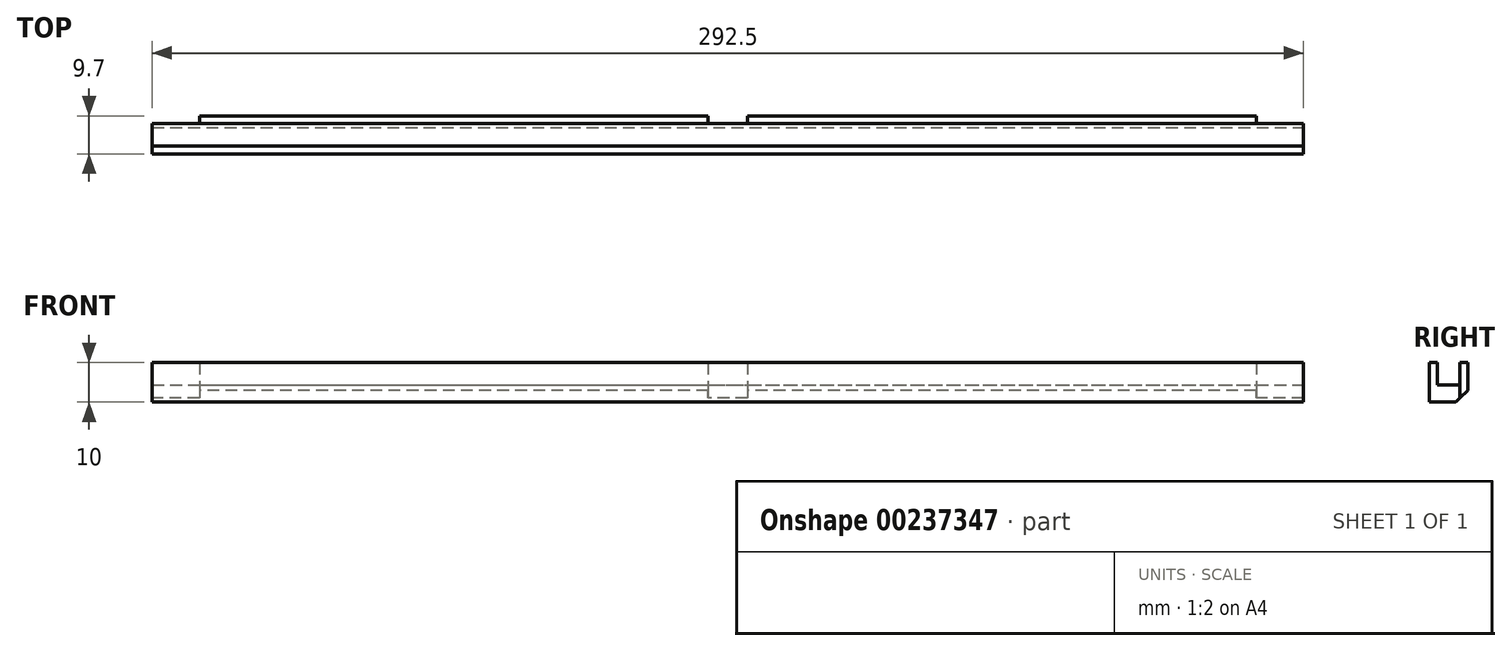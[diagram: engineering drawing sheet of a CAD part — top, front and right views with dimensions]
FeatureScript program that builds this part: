
annotation { "Feature Type Name" : "Feature", "Feature Type Description" : "" }
export const myFeature = defineFeature(function(context is Context, id is Id, definition is map)
    precondition{}
    {
        {
            var Q0;
            Q0=qCreatedBy(makeId("Top.planeOp"),FACE);
            var sketch = newSketch(context, id + "F0", { "sketchPlane" : qUnion([Q0])});
            skLineSegment(sketch, "E0.bottom", {"start": v(-146.25, 2.85) * mm, "end": v(146.25, 2.85) * mm});
            skLineSegment(sketch, "E0.top", {"start": v(-146.25, -2.85) * mm, "end": v(146.25, -2.85) * mm});
            skLineSegment(sketch, "E0.left", {"start": v(-146.25, 2.85) * mm, "end": v(-146.25, -2.85) * mm});
            skLineSegment(sketch, "E0.right", {"start": v(146.25, 2.85) * mm, "end": v(146.25, -2.85) * mm});
            skPoint(sketch, "E0.middle", {"position": v(0, 0) * mm});
            skLineSegment(sketch, "E1", {"start": v(-146.25, 2.85) * mm, "end": v(-146.25, 4.85) * mm});
            skLineSegment(sketch, "E2", {"start": v(-146.25, 4.85) * mm, "end": v(146.25, 4.85) * mm});
            skLineSegment(sketch, "E3", {"start": v(146.25, 4.85) * mm, "end": v(146.25, 2.85) * mm});
            skLineSegment(sketch, "E4", {"start": v(-146.25, -2.85) * mm, "end": v(-146.25, -4.85) * mm});
            skLineSegment(sketch, "E5", {"start": v(-146.25, -4.85) * mm, "end": v(146.25, -4.85) * mm});
            skLineSegment(sketch, "E6", {"start": v(146.25, -4.85) * mm, "end": v(146.25, -2.85) * mm});
            skLineSegment(sketch, "E7", {"start": v(0, 4.85) * mm, "end": v(0, -4.85) * mm});
            skLineSegment(sketch, "E8.bottom", {"start": v(-139.25, 2.85) * mm, "end": v(-134.25, 2.85) * mm});
            skLineSegment(sketch, "E8.top", {"start": v(-139.25, 4.85) * mm, "end": v(-134.25, 4.85) * mm});
            skLineSegment(sketch, "E8.left", {"start": v(-139.25, 2.85) * mm, "end": v(-139.25, 4.85) * mm});
            skLineSegment(sketch, "E8.right", {"start": v(-134.25, 2.85) * mm, "end": v(-134.25, 4.85) * mm});
            skLineSegment(sketch, "E9.MirrorCS", {"start": v(139.25, 2.85) * mm, "end": v(134.25, 2.85) * mm});
            skLineSegment(sketch, "E10.MirrorCS", {"start": v(139.25, 4.85) * mm, "end": v(134.25, 4.85) * mm});
            skLineSegment(sketch, "E11.MirrorCS", {"start": v(139.25, 2.85) * mm, "end": v(139.25, 4.85) * mm});
            skLineSegment(sketch, "E12.MirrorCS", {"start": v(134.25, 2.85) * mm, "end": v(134.25, 4.85) * mm});
            skLineSegment(sketch, "E13.bottom", {"start": v(5, 2.85) * mm, "end": v(-5, 2.85) * mm});
            skLineSegment(sketch, "E13.left", {"start": v(5, 2.85) * mm, "end": v(5, 4.85) * mm});
            skLineSegment(sketch, "E13.right", {"start": v(-5, 2.85) * mm, "end": v(-5, 4.85) * mm});
            skPoint(sketch, "E13.middle", {"position": v(0, 4.85) * mm});
            skLineSegment(sketch, "E14", {"start": v(-139.25, 4.85) * mm, "end": v(-139.25, 2.85) * mm});
            skLineSegment(sketch, "E15.MirrorCS", {"start": v(139.25, 4.85) * mm, "end": v(139.25, 2.85) * mm});
            skSolve(sketch);
        }
        {
            var Q0;
            {var subQ0=sQuery(id+"F0.wireOp",EDGE,"E0.right");Q0=makeQuery(id+"F0.imprint","IMPRINT",FACE,{"disambiguationData":[TD([[makeQuery(id+"F0.imprint","IMPRINT",EDGE,{"derivedFrom":subQ0}),-1.0]])]});}
            var Q1;
            {var subQ0=sQuery(id+"F0.wireOp",EDGE,"1EJgJWwb-nkAs-t9n1-ytm8-ceu9wyUzjA9J.bottom");Q1=makeQuery(id+"F0.imprint","IMPRINT",FACE,{"disambiguationData":[TD([[makeQuery(id+"F0.imprint","IMPRINT",EDGE,{"derivedFrom":subQ0}),-1.0]])]});}
            var Q2;
            {var subQ6=sQuery(id+"F0.wireOp",EDGE,"E0.left");Q2=makeQuery(id+"F0.imprint","IMPRINT",FACE,{"disambiguationData":[TD([[makeQuery(id+"F0.imprint","IMPRINT",EDGE,{"derivedFrom":subQ6}),1.0]])]});}
            extrude(context, id + "F1", {"entities" : qUnion([Q0, Q1, Q2]), "depth" : 4.3 * mm});
        }
        {
            var Q0;
            {var subQ0=sQuery(id+"F0.wireOp",EDGE,"E12.MirrorCS");Q0=makeQuery(id+"F0.imprint","IMPRINT",FACE,{"disambiguationData":[TD([[makeQuery(id+"F0.imprint","IMPRINT",EDGE,{"derivedFrom":subQ0}),1.0]])]});}
            var Q1;
            {var subQ0=sQuery(id+"F0.wireOp",EDGE,"E6");Q1=makeQuery(id+"F0.imprint","IMPRINT",FACE,{"disambiguationData":[TD([[makeQuery(id+"F0.imprint","IMPRINT",EDGE,{"derivedFrom":subQ0}),1.0]])]});}
            var Q2;
            {var subQ0=sQuery(id+"F0.wireOp",EDGE,"E4");Q2=makeQuery(id+"F0.imprint","IMPRINT",FACE,{"disambiguationData":[TD([[makeQuery(id+"F0.imprint","IMPRINT",EDGE,{"derivedFrom":subQ0}),1.0]])]});}
            var Q3;
            {var subQ0=sQuery(id+"F0.wireOp",EDGE,"E8.right");Q3=makeQuery(id+"F0.imprint","IMPRINT",FACE,{"disambiguationData":[TD([[makeQuery(id+"F0.imprint","IMPRINT",EDGE,{"derivedFrom":subQ0}),-1.0]])]});}
            extrude(context, id + "F2", {"entities" : qUnion([Q0, Q1, Q2, Q3]), "operationType" : NewBodyOperationType.ADD, "depth" : 10 * mm});
        }
        {
            var Q0;
            {var subQ0=sQuery(id+"F0.wireOp",EDGE,"E2");Q0=makeQuery(id+"F2.opExtrude","CAP_EDGE",EDGE,{"disambiguationData":[OSD([subQ0]),TDD([makeQuery(id+"F0.imprint","IMPRINT",EDGE,{"disambiguationData":[TD([[makeQuery(id+"F0.imprint","INTERSECT",VERTEX,{"derivedFrom":[subQ0,sQuery(id+"F0.wireOp",EDGE,"E13.left")]}),-1.0]])],"derivedFrom":subQ0})])],"isStart":true});}
            chamfer(context, id + "F3", {"entities" : qUnion([Q0]), "width" : 3 * mm, "tangentPropagation" : true});
        }
    });
